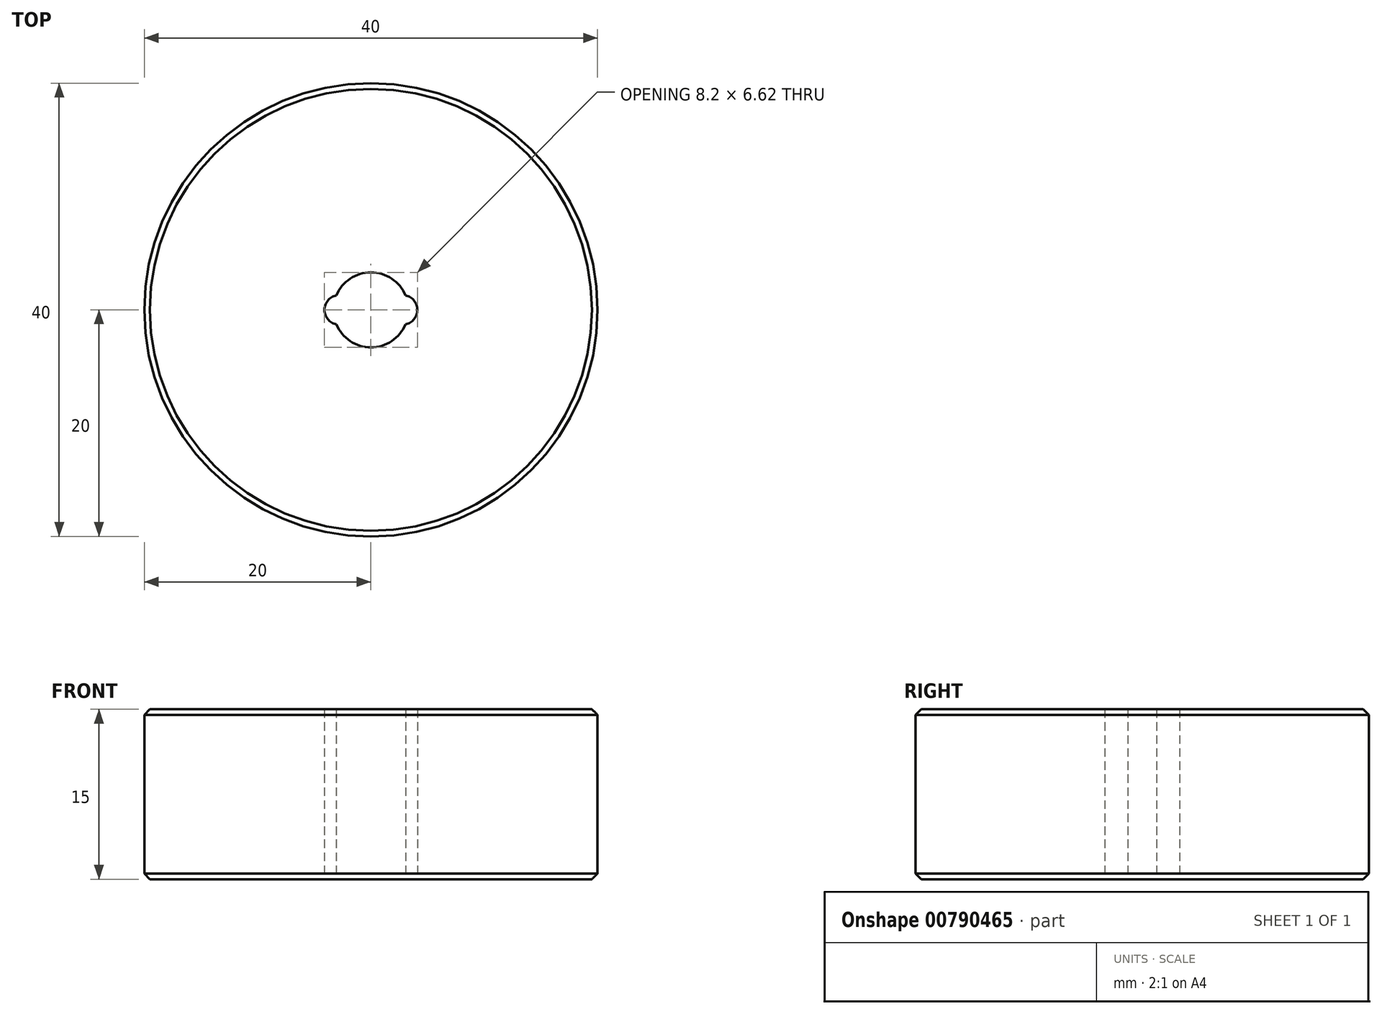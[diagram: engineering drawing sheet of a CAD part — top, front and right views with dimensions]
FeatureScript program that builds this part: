
annotation { "Feature Type Name" : "Feature", "Feature Type Description" : "" }
export const myFeature = defineFeature(function(context is Context, id is Id, definition is map)
    precondition{}
    {
        {
            var Q0;
            Q0=qCreatedBy(makeId("Top.planeOp"),FACE);
            var sketch = newSketch(context, id + "F0", { "sketchPlane" : qUnion([Q0])});
            skCircle(sketch, "E0", {"center": v(0, 0) * mm, "radius": 20 * mm});
            skArc(sketch, "E1", {"start": v(-3.05, -1.27) * mm, "mid": v(0, -3.31) * mm, "end": v(3.05, -1.27) * mm});
            skArc(sketch, "E2", {"start": v(-3.05, 1.27) * mm, "mid": v(-4.1, 0) * mm, "end": v(-3.05, -1.27) * mm});
            skArc(sketch, "E3", {"start": v(3.05, -1.27) * mm, "mid": v(4.1, 0) * mm, "end": v(3.05, 1.27) * mm});
            skArc(sketch, "E4.trimOffspring", {"start": v(3.05, 1.27) * mm, "mid": v(0, 3.3) * mm, "end": v(-3.05, 1.27) * mm});
            skSolve(sketch);
        }
        {
            var Q0;
            Q0=makeQuery(id+"F0.imprint","IMPRINT",FACE,{"disambiguationData":[TD([[makeQuery(id+"F0.imprint","IMPRINT",EDGE,{"derivedFrom":sQuery(id+"F0.wireOp",EDGE,"E0")}),1.0]])]});
            extrude(context, id + "F1", {"entities" : qUnion([Q0]), "depth" : 15 * mm, "offsetDistance" : 25 * mm});
        }
        {
            var Q0;
            Q0=makeQuery(id+"F1.opExtrude","CAP_EDGE",EDGE,{"disambiguationData":[OSD([sQuery(id+"F0.wireOp",EDGE,"E0")])],"isStart":false});
            var Q1;
            Q1=makeQuery(id+"F1.opExtrude","CAP_EDGE",EDGE,{"disambiguationData":[OSD([sQuery(id+"F0.wireOp",EDGE,"E0")])],"isStart":true});
            chamfer(context, id + "F2", {"entities" : qUnion([Q0, Q1]), "width" : .5 * mm, "tangentPropagation" : true});
        }
    });
